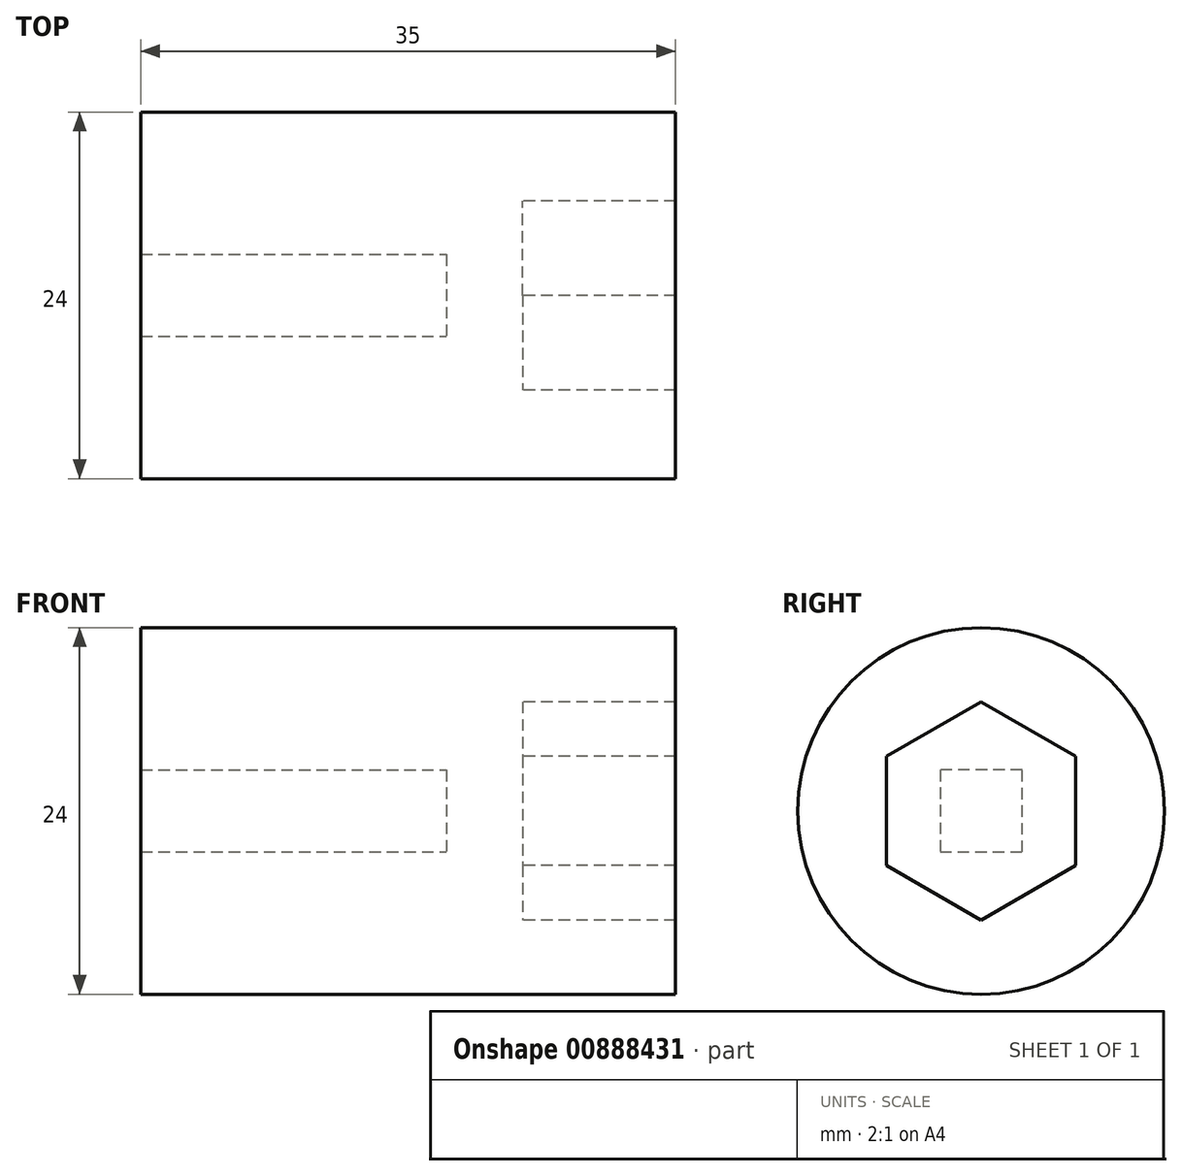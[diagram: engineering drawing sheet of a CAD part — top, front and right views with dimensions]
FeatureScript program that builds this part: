
annotation { "Feature Type Name" : "Feature", "Feature Type Description" : "" }
export const myFeature = defineFeature(function(context is Context, id is Id, definition is map)
    precondition{}
    {
        {
            var Q0;
            Q0=qCreatedBy(makeId("Right.planeOp"),FACE);
            var sketch = newSketch(context, id + "F0", { "sketchPlane" : qUnion([Q0])});
            skCircle(sketch, "E0", {"center": v(0, 0) * mm, "radius": 12 * mm});
            skCircle(sketch, "E1.cCircle", {"center": v(0, 0) * mm, "radius": 6.2 * mm, "construction": true});
            skLineSegment(sketch, "E1.0", {"start": v(6.2, 3.57) * mm, "end": v(6.2, -3.57) * mm});
            skLineSegment(sketch, "E1.1", {"start": v(6.19, -3.57) * mm, "end": v(0, -7.15) * mm});
            skLineSegment(sketch, "E1.2", {"start": v(0, -7.15) * mm, "end": v(-6.2, -3.57) * mm});
            skLineSegment(sketch, "E1.3", {"start": v(-6.19, -3.57) * mm, "end": v(-6.19, 3.57) * mm});
            skLineSegment(sketch, "E1.4", {"start": v(-6.2, 3.57) * mm, "end": v(0, 7.15) * mm});
            skLineSegment(sketch, "E1.5", {"start": v(0, 7.15) * mm, "end": v(6.19, 3.57) * mm});
            skPoint(sketch, "E1.0.midPoint", {"position": v(6.2, 0) * mm});
            skSolve(sketch);
        }
        {
            var Q0;
            Q0=makeQuery(id+"F0.imprint","IMPRINT",FACE,{"disambiguationData":[TD([[makeQuery(id+"F0.imprint","IMPRINT",EDGE,{"derivedFrom":sQuery(id+"F0.wireOp",EDGE,"E0")}),1.0]])]});
            extrude(context, id + "F1", {"entities" : qUnion([Q0]), "depth" : 10 * mm, "offsetDistance" : 25 * mm});
        }
        {
            var Q0;
            Q0=makeQuery(id+"F0.imprint","IMPRINT",FACE,{"disambiguationData":[TD([[makeQuery(id+"F0.imprint","IMPRINT",EDGE,{"derivedFrom":sQuery(id+"F0.wireOp",EDGE,"E0")}),1.0]])]});
            var Q1;
            Q1=makeQuery(id+"F0.imprint","IMPRINT",FACE,{"disambiguationData":[TD([[makeQuery(id+"F0.imprint","IMPRINT",EDGE,{"derivedFrom":sQuery(id+"F0.wireOp",EDGE,"E1.0")}),-1.0]])]});
            extrude(context, id + "F2", {"entities" : qUnion([Q0, Q1]), "operationType" : NewBodyOperationType.ADD, "oppositeDirection" : true, "depth" : 5 * mm, "offsetDistance" : 25 * mm});
        }
        {
            var Q0;
            Q0=makeQuery(id+"F2.opExtrude","CAP_FACE",FACE,{"disambiguationData":[OSD([sQuery(id+"F0.wireOp",EDGE,"E0")])],"isStart":false});
            var sketch = newSketch(context, id + "F3", { "sketchPlane" : qUnion([Q0])});
            skCircle(sketch, "E2.cCircle", {"center": v(0, 0) * mm, "radius": 2.69 * mm, "construction": true});
            skLineSegment(sketch, "E2.0", {"start": v(2.69, 2.69) * mm, "end": v(2.69, -2.69) * mm});
            skLineSegment(sketch, "E2.1", {"start": v(2.69, -2.69) * mm, "end": v(-2.69, -2.69) * mm});
            skLineSegment(sketch, "E2.2", {"start": v(-2.69, -2.69) * mm, "end": v(-2.69, 2.69) * mm});
            skLineSegment(sketch, "E2.3", {"start": v(-2.69, 2.69) * mm, "end": v(2.69, 2.69) * mm});
            skPoint(sketch, "E2.0.midPoint", {"position": v(2.69, 0) * mm});
            skSolve(sketch);
        }
        {
            var Q0;
            Q0=makeQuery(id+"F3.imprint","IMPRINT",FACE,{"disambiguationData":[TD([[makeQuery(id+"F3.imprint","IMPRINT",EDGE,{"derivedFrom":sQuery(id+"F3.wireOp",EDGE,"E2.0")}),1.0]])]});
            extrude(context, id + "F4", {"entities" : qUnion([Q0]), "operationType" : NewBodyOperationType.ADD, "depth" : 20 * mm, "offsetDistance" : 25 * mm});
        }
    });
